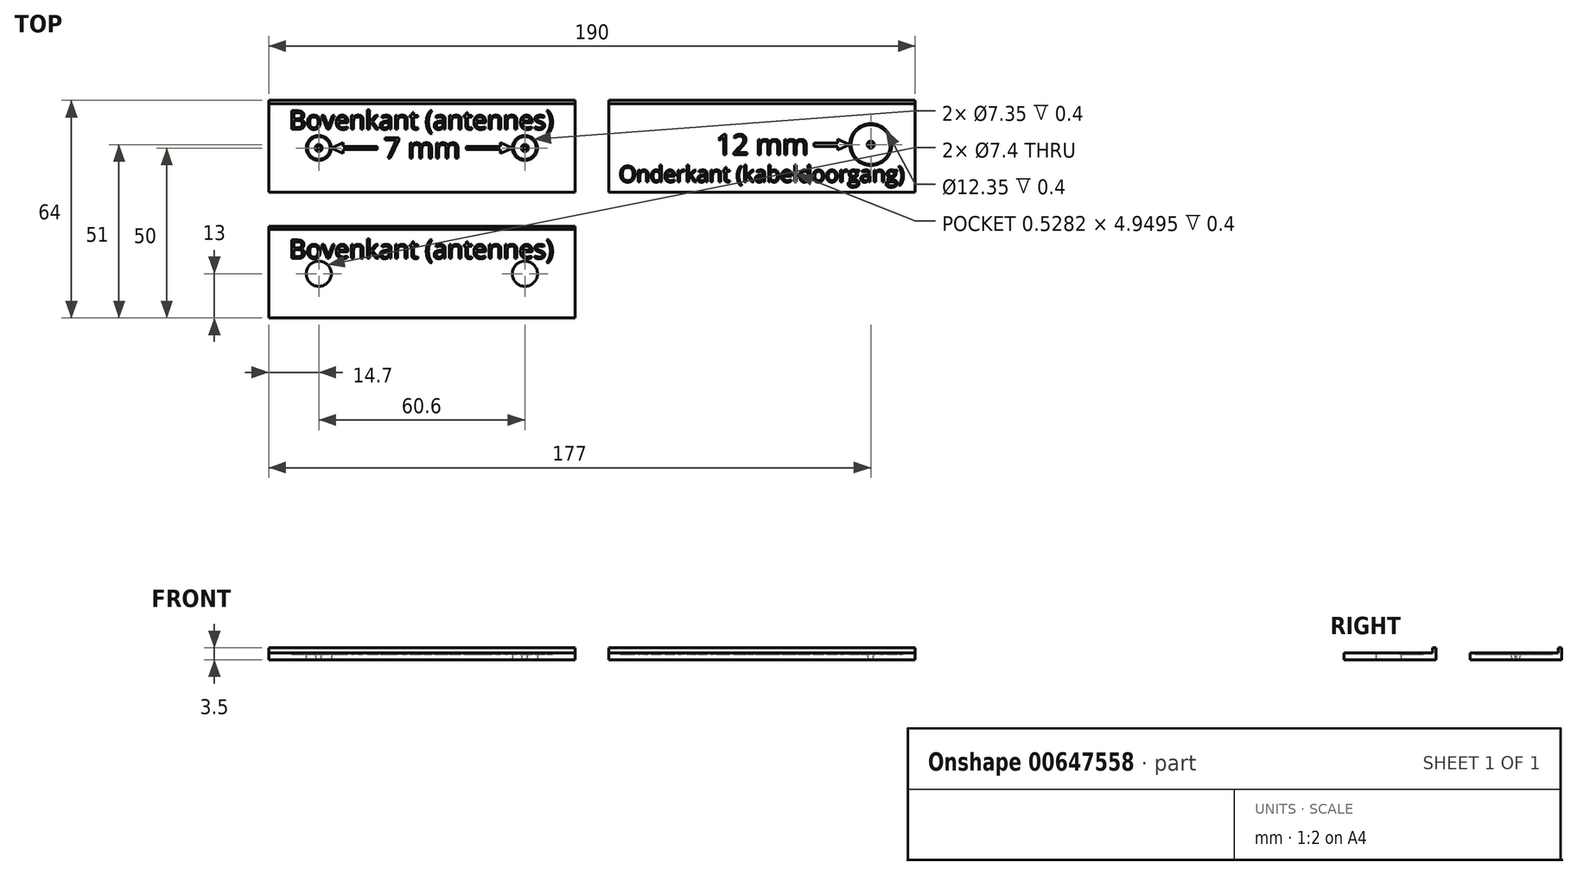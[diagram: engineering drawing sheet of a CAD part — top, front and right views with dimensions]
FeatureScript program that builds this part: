
annotation { "Feature Type Name" : "Feature", "Feature Type Description" : "" }
export const myFeature = defineFeature(function(context is Context, id is Id, definition is map)
    precondition{}
    {
        {
            var Q0;
            Q0=qCreatedBy(makeId("Top.planeOp"),FACE);
            var sketch = newSketch(context, id + "F0", { "sketchPlane" : qUnion([Q0])});
            skLineSegment(sketch, "E0.bottom", {"start": v(45, -13.5) * mm, "end": v(-45, -13.5) * mm});
            skLineSegment(sketch, "E0.top", {"start": v(45, 13.5) * mm, "end": v(-45, 13.5) * mm});
            skLineSegment(sketch, "E0.left", {"start": v(45, -13.5) * mm, "end": v(45, 13.5) * mm});
            skLineSegment(sketch, "E0.right", {"start": v(-45, -13.5) * mm, "end": v(-45, 13.5) * mm});
            skPoint(sketch, "E0.middle", {"position": v(0, 0) * mm});
            skLineSegment(sketch, "E1", {"start": v(-45, -0.5) * mm, "end": v(45, -0.5) * mm, "construction": true});
            skLineSegment(sketch, "E2", {"start": v(-30.3, 18.8) * mm, "end": v(30.3, 18.8) * mm, "construction": true});
            skPoint(sketch, "E3", {"position": v(0, 18.8) * mm});
            skPoint(sketch, "E4", {"position": v(-30.3, -0.5) * mm});
            skPoint(sketch, "E5", {"position": v(30.3, -0.5) * mm});
            skLineSegment(sketch, "E6.bottom", {"start": v(-45, -23.5) * mm, "end": v(45, -23.5) * mm});
            skLineSegment(sketch, "E6.top", {"start": v(-45, -50.5) * mm, "end": v(45, -50.5) * mm});
            skLineSegment(sketch, "E6.left", {"start": v(-45, -23.5) * mm, "end": v(-45, -50.5) * mm});
            skLineSegment(sketch, "E6.right", {"start": v(45, -23.5) * mm, "end": v(45, -50.5) * mm});
            skLineSegment(sketch, "E7", {"start": v(-45, -37.5) * mm, "end": v(45, -37.5) * mm, "construction": true});
            skCircle(sketch, "E8", {"center": v(-30.3, -37.5) * mm, "radius": 3.7 * mm});
            skCircle(sketch, "E9", {"center": v(30.3, -37.5) * mm, "radius": 3.7 * mm});
            skLineSegment(sketch, "E10.bottom", {"start": v(55, -13.5) * mm, "end": v(145, -13.5) * mm});
            skLineSegment(sketch, "E10.top", {"start": v(55, 13.5) * mm, "end": v(145, 13.5) * mm});
            skLineSegment(sketch, "E10.left", {"start": v(55, -13.5) * mm, "end": v(55, 13.5) * mm});
            skLineSegment(sketch, "E10.right", {"start": v(145, -13.5) * mm, "end": v(145, 13.5) * mm});
            skLineSegment(sketch, "E11", {"start": v(55, 0.5) * mm, "end": v(145, 0.5) * mm, "construction": true});
            skPoint(sketch, "E12", {"position": v(68, 0.5) * mm});
            skPoint(sketch, "E13", {"position": v(132, 0.5) * mm});
            skSolve(sketch);
        }
        {
            var Q0;
            Q0=makeQuery(id+"F0.imprint","IMPRINT",FACE,{"disambiguationData":[TD([[makeQuery(id+"F0.imprint","IMPRINT",EDGE,{"derivedFrom":sQuery(id+"F0.wireOp",EDGE,"E0.bottom")}),-1.0]])]});
            var Q1;
            Q1=makeQuery(id+"F0.imprint","IMPRINT",FACE,{"disambiguationData":[TD([[makeQuery(id+"F0.imprint","IMPRINT",EDGE,{"derivedFrom":sQuery(id+"F0.wireOp",EDGE,"E6.bottom")}),-1.0]])]});
            var Q2;
            Q2=makeQuery(id+"F0.imprint","IMPRINT",FACE,{"disambiguationData":[TD([[makeQuery(id+"F0.imprint","IMPRINT",EDGE,{"derivedFrom":sQuery(id+"F0.wireOp",EDGE,"E10.bottom")}),1.0]])]});
            extrude(context, id + "F1", {"entities" : qUnion([Q0, Q1, Q2]), "depth" : 2 * mm, "offsetDistance" : 25 * mm});
        }
        {
            var Q0;
            Q0=makeQuery(id+"F1.opExtrude","CAP_FACE",FACE,{"disambiguationData":[OSD([sQuery(id+"F0.wireOp",EDGE,"E0.bottom"),sQuery(id+"F0.wireOp",EDGE,"E0.top"),sQuery(id+"F0.wireOp",EDGE,"E0.left"),sQuery(id+"F0.wireOp",EDGE,"E0.right")])],"isStart":false});
            var sketch = newSketch(context, id + "F2", { "sketchPlane" : qUnion([Q0])});
            skLineSegment(sketch, "E14.0.0", {"start": v(-45, -13.5) * mm, "end": v(45, -13.5) * mm});
            skLineSegment(sketch, "E14.0.1", {"start": v(45, -13.5) * mm, "end": v(45, 13.5) * mm});
            skLineSegment(sketch, "E14.0.2", {"start": v(45, 13.5) * mm, "end": v(-45, 13.5) * mm});
            skLineSegment(sketch, "E14.0.3", {"start": v(-45, 13.5) * mm, "end": v(-45, -13.5) * mm});
            skPoint(sketch, "E15.0", {"position": v(-30.3, -0.5) * mm});
            skPoint(sketch, "E16.0", {"position": v(30.3, -0.5) * mm});
            skCircle(sketch, "E17", {"center": v(-30.3, -0.5) * mm, "radius": 1.05 * mm});
            skCircle(sketch, "E18", {"center": v(30.3, -0.5) * mm, "radius": 1.05 * mm});
            skText(sketch, "E19", { "text": "Bovenkant (antennes)", "fontName": "OpenSans-Regular.ttf"});
            skCircle(sketch, "E20", {"center": v(-30.3, -0.5) * mm, "radius": 3.33 * mm});
            skCircle(sketch, "E21", {"center": v(-30.3, -0.5) * mm, "radius": 3.67 * mm});
            skCircle(sketch, "E22", {"center": v(30.3, -0.5) * mm, "radius": 3.33 * mm});
            skCircle(sketch, "E23", {"center": v(30.3, -0.5) * mm, "radius": 3.67 * mm});
            skLineSegment(sketch, "E24", {"start": v(-45, 12.5) * mm, "end": v(45, 12.5) * mm});
            skLineSegment(sketch, "E25.0.0", {"start": v(45, -23.5) * mm, "end": v(-45, -23.5) * mm});
            skLineSegment(sketch, "E25.0.1", {"start": v(-45, -23.5) * mm, "end": v(-45, -50.5) * mm});
            skLineSegment(sketch, "E25.0.2", {"start": v(-45, -50.5) * mm, "end": v(45, -50.5) * mm});
            skLineSegment(sketch, "E25.0.3", {"start": v(45, -50.5) * mm, "end": v(45, -23.5) * mm});
            skLineSegment(sketch, "E26", {"start": v(-45, -24.5) * mm, "end": v(45, -24.5) * mm});
            skText(sketch, "E27", { "text": "Bovenkant (antennes)", "fontName": "OpenSans-Regular.ttf"});
            skText(sketch, "E28", { "text": "7 mm", "fontName": "OpenSans-Regular.ttf"});
            skPoint(sketch, "E29", {"position": v(0, -0.5) * mm});
            skLineSegment(sketch, "E30", {"start": v(-30.3, -0.5) * mm, "end": v(30.3, -0.5) * mm, "construction": true});
            skLineSegment(sketch, "E31", {"start": v(-26.6, -0.5) * mm, "end": v(-23.1, 1.13) * mm});
            skLineSegment(sketch, "E32", {"start": v(-26.6, -0.5) * mm, "end": v(-23.1, -2.13) * mm});
            skLineSegment(sketch, "E33", {"start": v(-23.1, 1.13) * mm, "end": v(-23.1, 0) * mm});
            skLineSegment(sketch, "E34", {"start": v(-23.1, 0) * mm, "end": v(-13.1, 0) * mm});
            skLineSegment(sketch, "E35", {"start": v(-13.1, 0) * mm, "end": v(-13.1, -1) * mm});
            skLineSegment(sketch, "E36", {"start": v(-13.1, -1) * mm, "end": v(-23.1, -1) * mm});
            skPoint(sketch, "E37", {"position": v(-13.1, -0.5) * mm});
            skLineSegment(sketch, "E38.trimOffspring", {"start": v(-23.1, -1) * mm, "end": v(-23.1, -2.13) * mm});
            skLineSegment(sketch, "E39.MirrorCS", {"start": v(26.6, -0.5) * mm, "end": v(23.1, 1.13) * mm});
            skLineSegment(sketch, "E40.MirrorCS", {"start": v(26.6, -0.5) * mm, "end": v(23.1, -2.13) * mm});
            skLineSegment(sketch, "E41.MirrorCS", {"start": v(13.1, -1) * mm, "end": v(23.1, -1) * mm});
            skLineSegment(sketch, "E42.MirrorCS", {"start": v(23.1, 0) * mm, "end": v(13.1, 0) * mm});
            skLineSegment(sketch, "E43.MirrorCS", {"start": v(13.1, 0) * mm, "end": v(13.1, -1) * mm});
            skLineSegment(sketch, "E44.MirrorCS", {"start": v(23.1, -1) * mm, "end": v(23.1, -2.13) * mm});
            skLineSegment(sketch, "E45.MirrorCS", {"start": v(23.1, 1.13) * mm, "end": v(23.1, 0) * mm});
            skPoint(sketch, "E46.0", {"position": v(68, 0.5) * mm});
            skPoint(sketch, "E47.0", {"position": v(132, 0.5) * mm});
            skLineSegment(sketch, "E48.0.0", {"start": v(55, 13.5) * mm, "end": v(55, -13.5) * mm});
            skLineSegment(sketch, "E48.0.1", {"start": v(55, -13.5) * mm, "end": v(145, -13.5) * mm});
            skLineSegment(sketch, "E48.0.2", {"start": v(145, -13.5) * mm, "end": v(145, 13.5) * mm});
            skLineSegment(sketch, "E48.0.3", {"start": v(145, 13.5) * mm, "end": v(55, 13.5) * mm});
            skLineSegment(sketch, "E49", {"start": v(55, 12.5) * mm, "end": v(145, 12.5) * mm});
            skText(sketch, "E50", { "text": "Onderkant (kabeldoorgang)", "fontName": "OpenSans-Regular.ttf"});
            skCircle(sketch, "E51", {"center": v(132, 0.5) * mm, "radius": 5.83 * mm});
            skCircle(sketch, "E52", {"center": v(132, 0.5) * mm, "radius": 6.17 * mm});
            skCircle(sketch, "E53", {"center": v(132, 0.5) * mm, "radius": 1.05 * mm});
            skLineSegment(sketch, "E54", {"start": v(125.75, 0.5) * mm, "end": v(122.25, 2.13) * mm});
            skLineSegment(sketch, "E55", {"start": v(125.75, 0.5) * mm, "end": v(122.25, -1.13) * mm});
            skLineSegment(sketch, "E56", {"start": v(122.25, 2.13) * mm, "end": v(122.25, 1) * mm});
            skLineSegment(sketch, "E57", {"start": v(122.25, 1) * mm, "end": v(115.25, 1) * mm});
            skLineSegment(sketch, "E58", {"start": v(115.25, 1) * mm, "end": v(115.25, 0) * mm});
            skLineSegment(sketch, "E59", {"start": v(115.25, 0) * mm, "end": v(122.25, 0) * mm});
            skPoint(sketch, "E60", {"position": v(115.25, 0.5) * mm});
            skPoint(sketch, "E61", {"position": v(122.25, 0.5) * mm});
            skLineSegment(sketch, "E62.trimOffspring", {"start": v(122.25, 0) * mm, "end": v(122.25, -1.13) * mm});
            skText(sketch, "E63", { "text": "12 mm", "fontName": "OpenSans-Regular.ttf"});
            skPoint(sketch, "E64", {"position": v(100, 0.5) * mm});
            skPoint(sketch, "E65", {"position": v(100, 12.5) * mm});
            const initialGuessF2  = {"E19": [-0.039, 0.005, 1, 0, 0.0055], "E27": [-0.039, -0.033, 1, 0, 0.0055], "E28": [-0.01115, -0.0035, 1, 0, 0.006], "E50": [0.058, -0.0105, 1, 0, 0.00469], "E63": [0.08647, -0.0025, 1, 0, 0.006]};
            skSetInitialGuess(sketch, initialGuessF2);
            skSolve(sketch);
        }
        {
            var Q0;
            Q0=makeQuery(id+"F2.imprint","IMPRINT",FACE,{"disambiguationData":[TD([[makeQuery(id+"F2.imprint","IMPRINT",EDGE,{"derivedFrom":sQuery(id+"F2.wireOp",EDGE,"E17")}),1.0]])]});
            var Q1;
            Q1=makeQuery(id+"F2.imprint","IMPRINT",FACE,{"disambiguationData":[TD([[makeQuery(id+"F2.imprint","IMPRINT",EDGE,{"derivedFrom":sQuery(id+"F2.wireOp",EDGE,"E18")}),1.0]])]});
            var Q2;
            Q2=makeQuery(id+"F2.imprint","IMPRINT",FACE,{"disambiguationData":[TD([[makeQuery(id+"F2.imprint","IMPRINT",EDGE,{"derivedFrom":sQuery(id+"F2.wireOp",EDGE,"E53")}),1.0]])]});
            extrude(context, id + "F3", {"entities" : qUnion([Q0, Q1, Q2]), "operationType" : NewBodyOperationType.REMOVE, "oppositeDirection" : true, "depth" : 25 * mm, "offsetDistance" : 25 * mm, "hasDraft" : true, "draftAngle" : 14 * degree, "draftPullDirection" : true});
        }
        {
            var Q0;
            Q0=makeQuery(id+"F2.imprint","IMPRINT",FACE,{"disambiguationData":[TD([[makeQuery(id+"F2.imprint","IMPRINT",EDGE,{"derivedFrom":sQuery(id+"F2.wireOp",EDGE,"E19.sketch_text.stroke-292")}),-1.0]])]});
            var Q1;
            Q1=makeQuery(id+"F2.imprint","IMPRINT",FACE,{"disambiguationData":[TD([[makeQuery(id+"F2.imprint","IMPRINT",EDGE,{"derivedFrom":sQuery(id+"F2.wireOp",EDGE,"E19.sketch_text.stroke-311")}),-1.0]])]});
            var Q2;
            Q2=makeQuery(id+"F2.imprint","IMPRINT",FACE,{"disambiguationData":[TD([[makeQuery(id+"F2.imprint","IMPRINT",EDGE,{"derivedFrom":sQuery(id+"F2.wireOp",EDGE,"E19.sketch_text.stroke-275")}),-1.0]])]});
            var Q3;
            Q3=makeQuery(id+"F2.imprint","IMPRINT",FACE,{"disambiguationData":[TD([[makeQuery(id+"F2.imprint","IMPRINT",EDGE,{"derivedFrom":sQuery(id+"F2.wireOp",EDGE,"E19.sketch_text.stroke-258")}),-1.0]])]});
            var Q4;
            Q4=makeQuery(id+"F2.imprint","IMPRINT",FACE,{"disambiguationData":[TD([[makeQuery(id+"F2.imprint","IMPRINT",EDGE,{"derivedFrom":sQuery(id+"F2.wireOp",EDGE,"E19.sketch_text.stroke-239")}),-1.0]])]});
            var Q5;
            Q5=makeQuery(id+"F2.imprint","IMPRINT",FACE,{"disambiguationData":[TD([[makeQuery(id+"F2.imprint","IMPRINT",EDGE,{"derivedFrom":sQuery(id+"F2.wireOp",EDGE,"E19.sketch_text.stroke-220")}),-1.0]])]});
            var Q6;
            Q6=makeQuery(id+"F2.imprint","IMPRINT",FACE,{"disambiguationData":[TD([[makeQuery(id+"F2.imprint","IMPRINT",EDGE,{"derivedFrom":sQuery(id+"F2.wireOp",EDGE,"E19.sketch_text.stroke-203")}),-1.0]])]});
            var Q7;
            Q7=makeQuery(id+"F2.imprint","IMPRINT",FACE,{"disambiguationData":[TD([[makeQuery(id+"F2.imprint","IMPRINT",EDGE,{"derivedFrom":sQuery(id+"F2.wireOp",EDGE,"E19.sketch_text.stroke-176")}),-1.0]])]});
            var Q8;
            Q8=makeQuery(id+"F2.imprint","IMPRINT",FACE,{"disambiguationData":[TD([[makeQuery(id+"F2.imprint","IMPRINT",EDGE,{"derivedFrom":sQuery(id+"F2.wireOp",EDGE,"E19.sketch_text.stroke-166")}),-1.0]])]});
            var Q9;
            Q9=makeQuery(id+"F2.imprint","IMPRINT",FACE,{"disambiguationData":[TD([[makeQuery(id+"F2.imprint","IMPRINT",EDGE,{"derivedFrom":sQuery(id+"F2.wireOp",EDGE,"E19.sketch_text.stroke-147")}),-1.0]])]});
            var Q10;
            Q10=makeQuery(id+"F2.imprint","IMPRINT",FACE,{"disambiguationData":[TD([[makeQuery(id+"F2.imprint","IMPRINT",EDGE,{"derivedFrom":sQuery(id+"F2.wireOp",EDGE,"E19.sketch_text.stroke-130")}),-1.0]])]});
            var Q11;
            Q11=makeQuery(id+"F2.imprint","IMPRINT",FACE,{"disambiguationData":[TD([[makeQuery(id+"F2.imprint","IMPRINT",EDGE,{"derivedFrom":sQuery(id+"F2.wireOp",EDGE,"E19.sketch_text.stroke-103")}),-1.0]])]});
            var Q12;
            Q12=makeQuery(id+"F2.imprint","IMPRINT",FACE,{"disambiguationData":[TD([[makeQuery(id+"F2.imprint","IMPRINT",EDGE,{"derivedFrom":sQuery(id+"F2.wireOp",EDGE,"E19.sketch_text.stroke-88")}),-1.0]])]});
            var Q13;
            Q13=makeQuery(id+"F2.imprint","IMPRINT",FACE,{"disambiguationData":[TD([[makeQuery(id+"F2.imprint","IMPRINT",EDGE,{"derivedFrom":sQuery(id+"F2.wireOp",EDGE,"E19.sketch_text.stroke-52")}),-1.0]])]});
            var Q14;
            Q14=makeQuery(id+"F2.imprint","IMPRINT",FACE,{"disambiguationData":[TD([[makeQuery(id+"F2.imprint","IMPRINT",EDGE,{"derivedFrom":sQuery(id+"F2.wireOp",EDGE,"E19.sketch_text.stroke-71")}),-1.0]])]});
            var Q15;
            Q15=makeQuery(id+"F2.imprint","IMPRINT",FACE,{"disambiguationData":[TD([[makeQuery(id+"F2.imprint","IMPRINT",EDGE,{"derivedFrom":sQuery(id+"F2.wireOp",EDGE,"E19.sketch_text.stroke-25")}),-1.0]])]});
            var Q16;
            Q16=makeQuery(id+"F2.imprint","IMPRINT",FACE,{"disambiguationData":[TD([[makeQuery(id+"F2.imprint","IMPRINT",EDGE,{"derivedFrom":sQuery(id+"F2.wireOp",EDGE,"E19.sketch_text.stroke-42")}),-1.0]])]});
            var Q17;
            Q17=makeQuery(id+"F2.imprint","IMPRINT",FACE,{"disambiguationData":[TD([[makeQuery(id+"F2.imprint","IMPRINT",EDGE,{"derivedFrom":sQuery(id+"F2.wireOp",EDGE,"E19.sketch_text.stroke-0")}),-1.0]])]});
            var Q18;
            Q18=makeQuery(id+"F2.imprint","IMPRINT",FACE,{"disambiguationData":[TD([[makeQuery(id+"F2.imprint","IMPRINT",EDGE,{"derivedFrom":sQuery(id+"F2.wireOp",EDGE,"E20")}),-1.0]])]});
            var Q19;
            Q19=makeQuery(id+"F2.imprint","IMPRINT",FACE,{"disambiguationData":[TD([[makeQuery(id+"F2.imprint","IMPRINT",EDGE,{"derivedFrom":sQuery(id+"F2.wireOp",EDGE,"E22")}),-1.0]])]});
            var Q20;
            Q20=makeQuery(id+"F2.imprint","IMPRINT",FACE,{"disambiguationData":[TD([[makeQuery(id+"F2.imprint","IMPRINT",EDGE,{"derivedFrom":sQuery(id+"F2.wireOp",EDGE,"E19.sketch_text.stroke-336")}),-1.0]])]});
            var Q21;
            Q21=makeQuery(id+"F2.imprint","IMPRINT",FACE,{"disambiguationData":[TD([[makeQuery(id+"F2.imprint","IMPRINT",EDGE,{"derivedFrom":sQuery(id+"F2.wireOp",EDGE,"E27.sketch_text.stroke-336")}),-1.0]])]});
            var Q22;
            Q22=makeQuery(id+"F2.imprint","IMPRINT",FACE,{"disambiguationData":[TD([[makeQuery(id+"F2.imprint","IMPRINT",EDGE,{"derivedFrom":sQuery(id+"F2.wireOp",EDGE,"E27.sketch_text.stroke-311")}),-1.0]])]});
            var Q23;
            Q23=makeQuery(id+"F2.imprint","IMPRINT",FACE,{"disambiguationData":[TD([[makeQuery(id+"F2.imprint","IMPRINT",EDGE,{"derivedFrom":sQuery(id+"F2.wireOp",EDGE,"E27.sketch_text.stroke-292")}),-1.0]])]});
            var Q24;
            Q24=makeQuery(id+"F2.imprint","IMPRINT",FACE,{"disambiguationData":[TD([[makeQuery(id+"F2.imprint","IMPRINT",EDGE,{"derivedFrom":sQuery(id+"F2.wireOp",EDGE,"E27.sketch_text.stroke-275")}),-1.0]])]});
            var Q25;
            Q25=makeQuery(id+"F2.imprint","IMPRINT",FACE,{"disambiguationData":[TD([[makeQuery(id+"F2.imprint","IMPRINT",EDGE,{"derivedFrom":sQuery(id+"F2.wireOp",EDGE,"E27.sketch_text.stroke-258")}),-1.0]])]});
            var Q26;
            Q26=makeQuery(id+"F2.imprint","IMPRINT",FACE,{"disambiguationData":[TD([[makeQuery(id+"F2.imprint","IMPRINT",EDGE,{"derivedFrom":sQuery(id+"F2.wireOp",EDGE,"E27.sketch_text.stroke-239")}),-1.0]])]});
            var Q27;
            Q27=makeQuery(id+"F2.imprint","IMPRINT",FACE,{"disambiguationData":[TD([[makeQuery(id+"F2.imprint","IMPRINT",EDGE,{"derivedFrom":sQuery(id+"F2.wireOp",EDGE,"E27.sketch_text.stroke-220")}),-1.0]])]});
            var Q28;
            Q28=makeQuery(id+"F2.imprint","IMPRINT",FACE,{"disambiguationData":[TD([[makeQuery(id+"F2.imprint","IMPRINT",EDGE,{"derivedFrom":sQuery(id+"F2.wireOp",EDGE,"E27.sketch_text.stroke-203")}),-1.0]])]});
            var Q29;
            Q29=makeQuery(id+"F2.imprint","IMPRINT",FACE,{"disambiguationData":[TD([[makeQuery(id+"F2.imprint","IMPRINT",EDGE,{"derivedFrom":sQuery(id+"F2.wireOp",EDGE,"E27.sketch_text.stroke-176")}),-1.0]])]});
            var Q30;
            Q30=makeQuery(id+"F2.imprint","IMPRINT",FACE,{"disambiguationData":[TD([[makeQuery(id+"F2.imprint","IMPRINT",EDGE,{"derivedFrom":sQuery(id+"F2.wireOp",EDGE,"E27.sketch_text.stroke-166")}),-1.0]])]});
            var Q31;
            Q31=makeQuery(id+"F2.imprint","IMPRINT",FACE,{"disambiguationData":[TD([[makeQuery(id+"F2.imprint","IMPRINT",EDGE,{"derivedFrom":sQuery(id+"F2.wireOp",EDGE,"E27.sketch_text.stroke-147")}),-1.0]])]});
            var Q32;
            Q32=makeQuery(id+"F2.imprint","IMPRINT",FACE,{"disambiguationData":[TD([[makeQuery(id+"F2.imprint","IMPRINT",EDGE,{"derivedFrom":sQuery(id+"F2.wireOp",EDGE,"E27.sketch_text.stroke-130")}),-1.0]])]});
            var Q33;
            Q33=makeQuery(id+"F2.imprint","IMPRINT",FACE,{"disambiguationData":[TD([[makeQuery(id+"F2.imprint","IMPRINT",EDGE,{"derivedFrom":sQuery(id+"F2.wireOp",EDGE,"E27.sketch_text.stroke-103")}),-1.0]])]});
            var Q34;
            Q34=makeQuery(id+"F2.imprint","IMPRINT",FACE,{"disambiguationData":[TD([[makeQuery(id+"F2.imprint","IMPRINT",EDGE,{"derivedFrom":sQuery(id+"F2.wireOp",EDGE,"E27.sketch_text.stroke-88")}),-1.0]])]});
            var Q35;
            Q35=makeQuery(id+"F2.imprint","IMPRINT",FACE,{"disambiguationData":[TD([[makeQuery(id+"F2.imprint","IMPRINT",EDGE,{"derivedFrom":sQuery(id+"F2.wireOp",EDGE,"E27.sketch_text.stroke-71")}),-1.0]])]});
            var Q36;
            Q36=makeQuery(id+"F2.imprint","IMPRINT",FACE,{"disambiguationData":[TD([[makeQuery(id+"F2.imprint","IMPRINT",EDGE,{"derivedFrom":sQuery(id+"F2.wireOp",EDGE,"E27.sketch_text.stroke-52")}),-1.0]])]});
            var Q37;
            Q37=makeQuery(id+"F2.imprint","IMPRINT",FACE,{"disambiguationData":[TD([[makeQuery(id+"F2.imprint","IMPRINT",EDGE,{"derivedFrom":sQuery(id+"F2.wireOp",EDGE,"E27.sketch_text.stroke-42")}),-1.0]])]});
            var Q38;
            Q38=makeQuery(id+"F2.imprint","IMPRINT",FACE,{"disambiguationData":[TD([[makeQuery(id+"F2.imprint","IMPRINT",EDGE,{"derivedFrom":sQuery(id+"F2.wireOp",EDGE,"E27.sketch_text.stroke-25")}),-1.0]])]});
            var Q39;
            Q39=makeQuery(id+"F2.imprint","IMPRINT",FACE,{"disambiguationData":[TD([[makeQuery(id+"F2.imprint","IMPRINT",EDGE,{"derivedFrom":sQuery(id+"F2.wireOp",EDGE,"E27.sketch_text.stroke-0")}),-1.0]])]});
            var Q40;
            Q40=makeQuery(id+"F2.imprint","IMPRINT",FACE,{"disambiguationData":[TD([[makeQuery(id+"F2.imprint","IMPRINT",EDGE,{"derivedFrom":sQuery(id+"F2.wireOp",EDGE,"E31")}),-1.0]])]});
            var Q41;
            Q41=makeQuery(id+"F2.imprint","IMPRINT",FACE,{"disambiguationData":[TD([[makeQuery(id+"F2.imprint","IMPRINT",EDGE,{"derivedFrom":sQuery(id+"F2.wireOp",EDGE,"E28.sketch_text.stroke-0")}),-1.0]])]});
            var Q42;
            Q42=makeQuery(id+"F2.imprint","IMPRINT",FACE,{"disambiguationData":[TD([[makeQuery(id+"F2.imprint","IMPRINT",EDGE,{"derivedFrom":sQuery(id+"F2.wireOp",EDGE,"E28.sketch_text.stroke-7")}),-1.0]])]});
            var Q43;
            Q43=makeQuery(id+"F2.imprint","IMPRINT",FACE,{"disambiguationData":[TD([[makeQuery(id+"F2.imprint","IMPRINT",EDGE,{"derivedFrom":sQuery(id+"F2.wireOp",EDGE,"E28.sketch_text.stroke-35")}),-1.0]])]});
            var Q44;
            Q44=makeQuery(id+"F2.imprint","IMPRINT",FACE,{"disambiguationData":[TD([[makeQuery(id+"F2.imprint","IMPRINT",EDGE,{"derivedFrom":sQuery(id+"F2.wireOp",EDGE,"E39.MirrorCS")}),1.0]])]});
            var Q45;
            Q45=makeQuery(id+"F2.imprint","IMPRINT",FACE,{"disambiguationData":[TD([[makeQuery(id+"F2.imprint","IMPRINT",EDGE,{"derivedFrom":sQuery(id+"F2.wireOp",EDGE,"E54")}),1.0]])]});
            var Q46;
            Q46=makeQuery(id+"F2.imprint","IMPRINT",FACE,{"disambiguationData":[TD([[makeQuery(id+"F2.imprint","IMPRINT",EDGE,{"derivedFrom":sQuery(id+"F2.wireOp",EDGE,"E51")}),-1.0]])]});
            var Q47;
            Q47=makeQuery(id+"F2.imprint","IMPRINT",FACE,{"disambiguationData":[TD([[makeQuery(id+"F2.imprint","IMPRINT",EDGE,{"derivedFrom":sQuery(id+"F2.wireOp",EDGE,"E63.sketch_text.stroke-0")}),-1.0]])]});
            var Q48;
            Q48=makeQuery(id+"F2.imprint","IMPRINT",FACE,{"disambiguationData":[TD([[makeQuery(id+"F2.imprint","IMPRINT",EDGE,{"derivedFrom":sQuery(id+"F2.wireOp",EDGE,"E63.sketch_text.stroke-9")}),-1.0]])]});
            var Q49;
            Q49=makeQuery(id+"F2.imprint","IMPRINT",FACE,{"disambiguationData":[TD([[makeQuery(id+"F2.imprint","IMPRINT",EDGE,{"derivedFrom":sQuery(id+"F2.wireOp",EDGE,"E63.sketch_text.stroke-29")}),-1.0]])]});
            var Q50;
            Q50=makeQuery(id+"F2.imprint","IMPRINT",FACE,{"disambiguationData":[TD([[makeQuery(id+"F2.imprint","IMPRINT",EDGE,{"derivedFrom":sQuery(id+"F2.wireOp",EDGE,"E63.sketch_text.stroke-57")}),-1.0]])]});
            var Q51;
            Q51=makeQuery(id+"F2.imprint","IMPRINT",FACE,{"disambiguationData":[TD([[makeQuery(id+"F2.imprint","IMPRINT",EDGE,{"derivedFrom":sQuery(id+"F2.wireOp",EDGE,"E50.sketch_text.stroke-0")}),-1.0]])]});
            var Q52;
            Q52=makeQuery(id+"F2.imprint","IMPRINT",FACE,{"disambiguationData":[TD([[makeQuery(id+"F2.imprint","IMPRINT",EDGE,{"derivedFrom":sQuery(id+"F2.wireOp",EDGE,"E50.sketch_text.stroke-16")}),-1.0]])]});
            var Q53;
            Q53=makeQuery(id+"F2.imprint","IMPRINT",FACE,{"disambiguationData":[TD([[makeQuery(id+"F2.imprint","IMPRINT",EDGE,{"derivedFrom":sQuery(id+"F2.wireOp",EDGE,"E50.sketch_text.stroke-33")}),-1.0]])]});
            var Q54;
            Q54=makeQuery(id+"F2.imprint","IMPRINT",FACE,{"disambiguationData":[TD([[makeQuery(id+"F2.imprint","IMPRINT",EDGE,{"derivedFrom":sQuery(id+"F2.wireOp",EDGE,"E50.sketch_text.stroke-57")}),-1.0]])]});
            var Q55;
            Q55=makeQuery(id+"F2.imprint","IMPRINT",FACE,{"disambiguationData":[TD([[makeQuery(id+"F2.imprint","IMPRINT",EDGE,{"derivedFrom":sQuery(id+"F2.wireOp",EDGE,"E50.sketch_text.stroke-76")}),-1.0]])]});
            var Q56;
            Q56=makeQuery(id+"F2.imprint","IMPRINT",FACE,{"disambiguationData":[TD([[makeQuery(id+"F2.imprint","IMPRINT",EDGE,{"derivedFrom":sQuery(id+"F2.wireOp",EDGE,"E50.sketch_text.stroke-89")}),-1.0]])]});
            var Q57;
            Q57=makeQuery(id+"F2.imprint","IMPRINT",FACE,{"disambiguationData":[TD([[makeQuery(id+"F2.imprint","IMPRINT",EDGE,{"derivedFrom":sQuery(id+"F2.wireOp",EDGE,"E50.sketch_text.stroke-104")}),-1.0]])]});
            var Q58;
            Q58=makeQuery(id+"F2.imprint","IMPRINT",FACE,{"disambiguationData":[TD([[makeQuery(id+"F2.imprint","IMPRINT",EDGE,{"derivedFrom":sQuery(id+"F2.wireOp",EDGE,"E50.sketch_text.stroke-131")}),-1.0]])]});
            var Q59;
            Q59=makeQuery(id+"F2.imprint","IMPRINT",FACE,{"disambiguationData":[TD([[makeQuery(id+"F2.imprint","IMPRINT",EDGE,{"derivedFrom":sQuery(id+"F2.wireOp",EDGE,"E50.sketch_text.stroke-148")}),-1.0]])]});
            var Q60;
            Q60=makeQuery(id+"F2.imprint","IMPRINT",FACE,{"disambiguationData":[TD([[makeQuery(id+"F2.imprint","IMPRINT",EDGE,{"derivedFrom":sQuery(id+"F2.wireOp",EDGE,"E50.sketch_text.stroke-167")}),-1.0]])]});
            var Q61;
            Q61=makeQuery(id+"F2.imprint","IMPRINT",FACE,{"disambiguationData":[TD([[makeQuery(id+"F2.imprint","IMPRINT",EDGE,{"derivedFrom":sQuery(id+"F2.wireOp",EDGE,"E50.sketch_text.stroke-177")}),-1.0]])]});
            var Q62;
            Q62=makeQuery(id+"F2.imprint","IMPRINT",FACE,{"disambiguationData":[TD([[makeQuery(id+"F2.imprint","IMPRINT",EDGE,{"derivedFrom":sQuery(id+"F2.wireOp",EDGE,"E50.sketch_text.stroke-192")}),-1.0]])]});
            var Q63;
            Q63=makeQuery(id+"F2.imprint","IMPRINT",FACE,{"disambiguationData":[TD([[makeQuery(id+"F2.imprint","IMPRINT",EDGE,{"derivedFrom":sQuery(id+"F2.wireOp",EDGE,"E50.sketch_text.stroke-219")}),-1.0]])]});
            var Q64;
            Q64=makeQuery(id+"F2.imprint","IMPRINT",FACE,{"disambiguationData":[TD([[makeQuery(id+"F2.imprint","IMPRINT",EDGE,{"derivedFrom":sQuery(id+"F2.wireOp",EDGE,"E50.sketch_text.stroke-242")}),-1.0]])]});
            var Q65;
            Q65=makeQuery(id+"F2.imprint","IMPRINT",FACE,{"disambiguationData":[TD([[makeQuery(id+"F2.imprint","IMPRINT",EDGE,{"derivedFrom":sQuery(id+"F2.wireOp",EDGE,"E50.sketch_text.stroke-261")}),-1.0]])]});
            var Q66;
            Q66=makeQuery(id+"F2.imprint","IMPRINT",FACE,{"disambiguationData":[TD([[makeQuery(id+"F2.imprint","IMPRINT",EDGE,{"derivedFrom":sQuery(id+"F2.wireOp",EDGE,"E50.sketch_text.stroke-265")}),-1.0]])]});
            var Q67;
            Q67=makeQuery(id+"F2.imprint","IMPRINT",FACE,{"disambiguationData":[TD([[makeQuery(id+"F2.imprint","IMPRINT",EDGE,{"derivedFrom":sQuery(id+"F2.wireOp",EDGE,"E50.sketch_text.stroke-289")}),-1.0]])]});
            var Q68;
            Q68=makeQuery(id+"F2.imprint","IMPRINT",FACE,{"disambiguationData":[TD([[makeQuery(id+"F2.imprint","IMPRINT",EDGE,{"derivedFrom":sQuery(id+"F2.wireOp",EDGE,"E50.sketch_text.stroke-306")}),-1.0]])]});
            var Q69;
            Q69=makeQuery(id+"F2.imprint","IMPRINT",FACE,{"disambiguationData":[TD([[makeQuery(id+"F2.imprint","IMPRINT",EDGE,{"derivedFrom":sQuery(id+"F2.wireOp",EDGE,"E50.sketch_text.stroke-323")}),-1.0]])]});
            var Q70;
            Q70=makeQuery(id+"F2.imprint","IMPRINT",FACE,{"disambiguationData":[TD([[makeQuery(id+"F2.imprint","IMPRINT",EDGE,{"derivedFrom":sQuery(id+"F2.wireOp",EDGE,"E50.sketch_text.stroke-336")}),-1.0]])]});
            var Q71;
            Q71=makeQuery(id+"F2.imprint","IMPRINT",FACE,{"disambiguationData":[TD([[makeQuery(id+"F2.imprint","IMPRINT",EDGE,{"derivedFrom":sQuery(id+"F2.wireOp",EDGE,"E50.sketch_text.stroke-380")}),-1.0]])]});
            var Q72;
            Q72=makeQuery(id+"F2.imprint","IMPRINT",FACE,{"disambiguationData":[TD([[makeQuery(id+"F2.imprint","IMPRINT",EDGE,{"derivedFrom":sQuery(id+"F2.wireOp",EDGE,"E50.sketch_text.stroke-407")}),-1.0]])]});
            var Q73;
            Q73=makeQuery(id+"F2.imprint","IMPRINT",FACE,{"disambiguationData":[TD([[makeQuery(id+"F2.imprint","IMPRINT",EDGE,{"derivedFrom":sQuery(id+"F2.wireOp",EDGE,"E50.sketch_text.stroke-424")}),-1.0]])]});
            var Q74;
            Q74=makeQuery(id+"F2.imprint","IMPRINT",FACE,{"disambiguationData":[TD([[makeQuery(id+"F2.imprint","IMPRINT",EDGE,{"derivedFrom":sQuery(id+"F2.wireOp",EDGE,"E50.sketch_text.stroke-468")}),-1.0]])]});
            extrude(context, id + "F4", {"entities" : qUnion([Q0, Q1, Q2, Q3, Q4, Q5, Q6, Q7, Q8, Q9, Q10, Q11, Q12, Q13, Q14, Q15, Q16, Q17, Q18, Q19, Q20, Q21, Q22, Q23, Q24, Q25, Q26, Q27, Q28, Q29, Q30, Q31, Q32, Q33, Q34, Q35, Q36, Q37, Q38, Q39, Q40, Q41, Q42, Q43, Q44, Q45, Q46, Q47, Q48, Q49, Q50, Q51, Q52, Q53, Q54, Q55, Q56, Q57, Q58, Q59, Q60, Q61, Q62, Q63, Q64, Q65, Q66, Q67, Q68, Q69, Q70, Q71, Q72, Q73, Q74]), "operationType" : NewBodyOperationType.REMOVE, "oppositeDirection" : true, "depth" : 0.4 * mm, "offsetDistance" : 25 * mm});
        }
        {
            var Q0;
            {var subQ0=sQuery(id+"F2.wireOp",EDGE,"E14.0.2");Q0=makeQuery(id+"F2.imprint","IMPRINT",FACE,{"disambiguationData":[TD([[makeQuery(id+"F2.imprint","IMPRINT",EDGE,{"derivedFrom":subQ0}),1.0]])]});}
            var Q1;
            {var subQ0=sQuery(id+"F2.wireOp",EDGE,"E25.0.0");Q1=makeQuery(id+"F2.imprint","IMPRINT",FACE,{"disambiguationData":[TD([[makeQuery(id+"F2.imprint","IMPRINT",EDGE,{"derivedFrom":subQ0}),1.0]])]});}
            var Q2;
            {var subQ0=sQuery(id+"F2.wireOp",EDGE,"E48.0.3");Q2=makeQuery(id+"F2.imprint","IMPRINT",FACE,{"disambiguationData":[TD([[makeQuery(id+"F2.imprint","IMPRINT",EDGE,{"derivedFrom":subQ0}),1.0]])]});}
            extrude(context, id + "F5", {"entities" : qUnion([Q0, Q1, Q2]), "operationType" : NewBodyOperationType.ADD, "depth" : 1.5 * mm, "offsetDistance" : 25 * mm});
        }
    });
